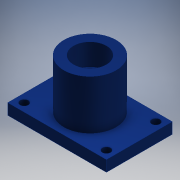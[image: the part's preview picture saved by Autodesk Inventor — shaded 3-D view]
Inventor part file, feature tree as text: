
AUTODESK INVENTOR PART (.ipt)
format: ipt  version: 2018 (Build 220112000, 112)  size: 129,536 bytes
history: native  units: mm
features: sketch x4, extrude x2, hole x2, other x1
ambient origin geometry x8: Origin, YZ Plane, XZ Plane, XY Plane, X Axis, Y Axis, Z Axis, Center Point
bodies: Body1 (feature_tree)
feature tree (9):
  other  "Sólido1"
  extrude  "Extrusión1"  Depth=24.0mm
  extrude  "Extrusión2"  Depth=30.0mm
  hole  "Agujero1"  [1 undecoded]
  hole  "Agujero2"  [1 undecoded]
  sketch  "Boceto1"  dims[d0=36.0mm d1=24.0mm]
  sketch  "Boceto2"  dims[d2=19.05mm d3=30.0mm]
  sketch  "Boceto3"  dims[d4=18.0mm d5=4.0mm d6=0.0mm]
  sketch  "Boceto4"  dims[d7=19.05mm d8=18.0mm d9=0.0mm d10=12.0mm d11=6.0mm d12=4.0mm d13=2.0mm d14=90.0deg d15=8.0mm d16=0.0mm d17=30.0mm d18=18.0mm d19=3.0mm d20=6.0mm d21=4.0mm d22=2.0mm d23=90.0deg d24=8.0mm d25=20.594885mm]
note: 2 required parameter values undecoded (feature->parameter linkage not recoverable at this tier; creation-order binding heuristic only, values carry confidence <= 0.55)
